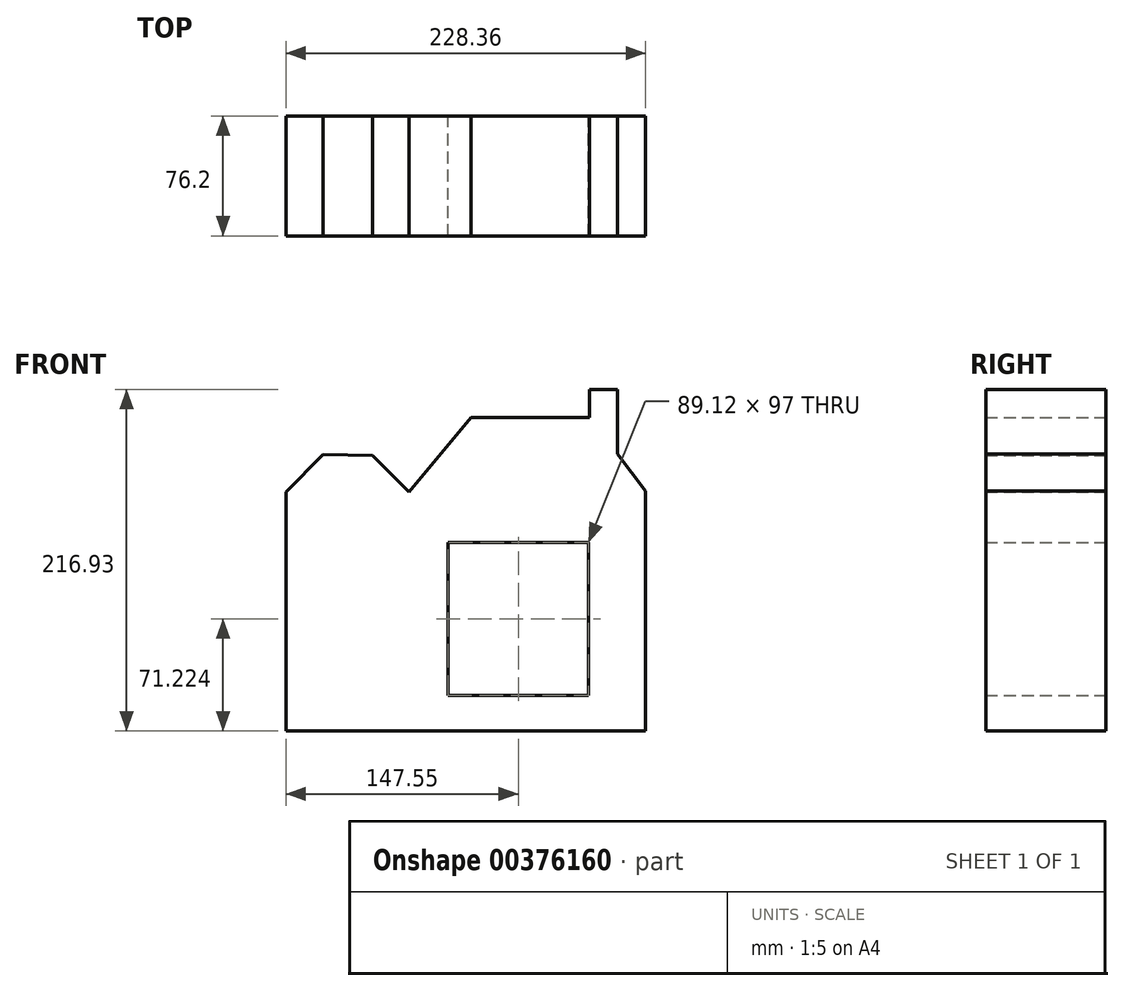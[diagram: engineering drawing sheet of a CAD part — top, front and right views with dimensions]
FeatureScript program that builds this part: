
annotation { "Feature Type Name" : "Feature", "Feature Type Description" : "" }
export const myFeature = defineFeature(function(context is Context, id is Id, definition is map)
    precondition{}
    {
        {
            var Q0;
            Q0=qCreatedBy(makeId("Front.planeOp"),FACE);
            var sketch = newSketch(context, id + "F0", { "sketchPlane" : qUnion([Q0])});
            skLineSegment(sketch, "E0", {"start": v(-74.97, 74.99) * mm, "end": v(-35.6, 122.53) * mm});
            skLineSegment(sketch, "E1", {"start": v(75.4, 75.78) * mm, "end": v(39.86, 122.53) * mm});
            skLineSegment(sketch, "E2", {"start": v(39.86, 122.53) * mm, "end": v(-39.5, 122.53) * mm});
            skLineSegment(sketch, "E3", {"start": v(57.63, 99.15) * mm, "end": v(57.63, 140.27) * mm});
            skLineSegment(sketch, "E4", {"start": v(57.63, 140.27) * mm, "end": v(39.86, 140.27) * mm});
            skLineSegment(sketch, "E5", {"start": v(39.86, 140.27) * mm, "end": v(39.86, 122.53) * mm});
            skLineSegment(sketch, "E6", {"start": v(75.4, 75.78) * mm, "end": v(-74.97, 74.99) * mm});
            skLineSegment(sketch, "E7", {"start": v(-74.97, 74.99) * mm, "end": v(-74.97, -76.66) * mm});
            skLineSegment(sketch, "E8", {"start": v(75.4, 75.78) * mm, "end": v(75.4, -76.66) * mm});
            skLineSegment(sketch, "E9", {"start": v(75.4, -76.66) * mm, "end": v(-74.97, -76.66) * mm});
            skLineSegment(sketch, "E10", {"start": v(-74.97, 74.99) * mm, "end": v(-152.96, 74.99) * mm});
            skLineSegment(sketch, "E11", {"start": v(-152.96, 74.99) * mm, "end": v(-152.96, -76.66) * mm});
            skLineSegment(sketch, "E12", {"start": v(-74.97, -76.66) * mm, "end": v(-152.96, -76.66) * mm});
            skLineSegment(sketch, "E13", {"start": v(-152.96, 74.99) * mm, "end": v(-129.5, 99.1) * mm});
            skLineSegment(sketch, "E14", {"start": v(-74.97, 74.99) * mm, "end": v(-98.12, 98.44) * mm});
            skLineSegment(sketch, "E15", {"start": v(-98.12, 98.44) * mm, "end": v(-129.5, 99.1) * mm});
            skLineSegment(sketch, "E16", {"start": v(-49.97, 43.07) * mm, "end": v(39.15, 43.07) * mm});
            skLineSegment(sketch, "E17", {"start": v(-49.97, 43.07) * mm, "end": v(-49.97, -53.94) * mm});
            skLineSegment(sketch, "E18", {"start": v(39.15, 43.07) * mm, "end": v(39.15, -53.94) * mm});
            skLineSegment(sketch, "E19", {"start": v(39.15, -53.94) * mm, "end": v(-49.97, -53.94) * mm});
            skSolve(sketch);
        }
        {
            var Q0;
            Q0 = qSketchRegion(id + "F0", true);
            extrude(context, id + "F1", {"entities" : qUnion([Q0]), "depth" : 25.4 * mm});
        }
        {
            var Q0;
            Q0 = qSketchRegion(id + "F0", true);
            extrude(context, id + "F2", {"entities" : qUnion([Q0]), "operationType" : NewBodyOperationType.ADD, "depth" : 25.4 * mm});
        }
        {
            var Q0;
            Q0 = qSketchRegion(id + "F0", true);
            extrude(context, id + "F3", {"entities" : qUnion([Q0]), "operationType" : NewBodyOperationType.ADD, "oppositeDirection" : true, "depth" : 25.4 * mm});
        }
        {
            var Q0;
            Q0 = qSketchRegion(id + "F0", true);
            extrude(context, id + "F4", {"entities" : qUnion([Q0]), "operationType" : NewBodyOperationType.ADD, "oppositeDirection" : true, "depth" : 25.4 * mm});
        }
        {
            var Q0;
            {var subQ2=sQuery(id+"F0.wireOp",EDGE,"E3");Q0=makeQuery(id+"F0.imprint","IMPRINT",FACE,{"disambiguationData":[TD([[makeQuery(id+"F0.imprint","IMPRINT",EDGE,{"derivedFrom":subQ2}),1.0]])]});}
            var Q1;
            Q1=makeQuery(id+"F0.imprint","IMPRINT",FACE,{"disambiguationData":[TD([[makeQuery(id+"F0.imprint","IMPRINT",EDGE,{"derivedFrom":sQuery(id+"F0.wireOp",EDGE,"E10")}),-1.0]])]});
            var Q2;
            {var subQ3=sQuery(id+"F0.wireOp",EDGE,"E0");Q2=makeQuery(id+"F0.imprint","IMPRINT",FACE,{"disambiguationData":[TD([[makeQuery(id+"F0.imprint","IMPRINT",EDGE,{"derivedFrom":subQ3}),-1.0]])]});}
            var Q3;
            Q3=makeQuery(id+"F0.imprint","IMPRINT",FACE,{"disambiguationData":[TD([[makeQuery(id+"F0.imprint","IMPRINT",EDGE,{"derivedFrom":sQuery(id+"F0.wireOp",EDGE,"E7")}),-1.0]])]});
            var Q4;
            Q4=makeQuery(id+"F0.imprint","IMPRINT",FACE,{"disambiguationData":[TD([[makeQuery(id+"F0.imprint","IMPRINT",EDGE,{"derivedFrom":sQuery(id+"F0.wireOp",EDGE,"E6")}),1.0]])]});
            var Q5;
            Q5=makeQuery(id+"F1.opExtrude","CAP_FACE",FACE,{"disambiguationData":[OSD([sQuery(id+"F0.wireOp",EDGE,"E1"),sQuery(id+"F0.wireOp",EDGE,"E2"),sQuery(id+"F0.wireOp",EDGE,"E3"),sQuery(id+"F0.wireOp",EDGE,"E4"),sQuery(id+"F0.wireOp",EDGE,"E5"),sQuery(id+"F0.wireOp",EDGE,"E0"),sQuery(id+"F0.wireOp",EDGE,"E8"),sQuery(id+"F0.wireOp",EDGE,"E9"),sQuery(id+"F0.wireOp",EDGE,"E11"),sQuery(id+"F0.wireOp",EDGE,"E12"),sQuery(id+"F0.wireOp",EDGE,"E13"),sQuery(id+"F0.wireOp",EDGE,"E14"),sQuery(id+"F0.wireOp",EDGE,"E15"),sQuery(id+"F0.wireOp",EDGE,"E16"),sQuery(id+"F0.wireOp",EDGE,"E17"),sQuery(id+"F0.wireOp",EDGE,"E18"),sQuery(id+"F0.wireOp",EDGE,"E19")])],"isStart":false});
            var Q6;
            Q6=makeQuery(id+"F3.opExtrude","CAP_FACE",FACE,{"disambiguationData":[OSD([sQuery(id+"F0.wireOp",EDGE,"E1"),sQuery(id+"F0.wireOp",EDGE,"E2"),sQuery(id+"F0.wireOp",EDGE,"E3"),sQuery(id+"F0.wireOp",EDGE,"E4"),sQuery(id+"F0.wireOp",EDGE,"E5"),sQuery(id+"F0.wireOp",EDGE,"E0"),sQuery(id+"F0.wireOp",EDGE,"E8"),sQuery(id+"F0.wireOp",EDGE,"E9"),sQuery(id+"F0.wireOp",EDGE,"E11"),sQuery(id+"F0.wireOp",EDGE,"E12"),sQuery(id+"F0.wireOp",EDGE,"E13"),sQuery(id+"F0.wireOp",EDGE,"E14"),sQuery(id+"F0.wireOp",EDGE,"E15"),sQuery(id+"F0.wireOp",EDGE,"E16"),sQuery(id+"F0.wireOp",EDGE,"E17"),sQuery(id+"F0.wireOp",EDGE,"E18"),sQuery(id+"F0.wireOp",EDGE,"E19")])],"isStart":false});
            extrude(context, id + "F5", {"entities" : qUnion([Q0, Q1, Q2, Q3, Q4, Q5, Q6]), "operationType" : NewBodyOperationType.ADD, "depth" : 25.4 * mm});
        }
    });
